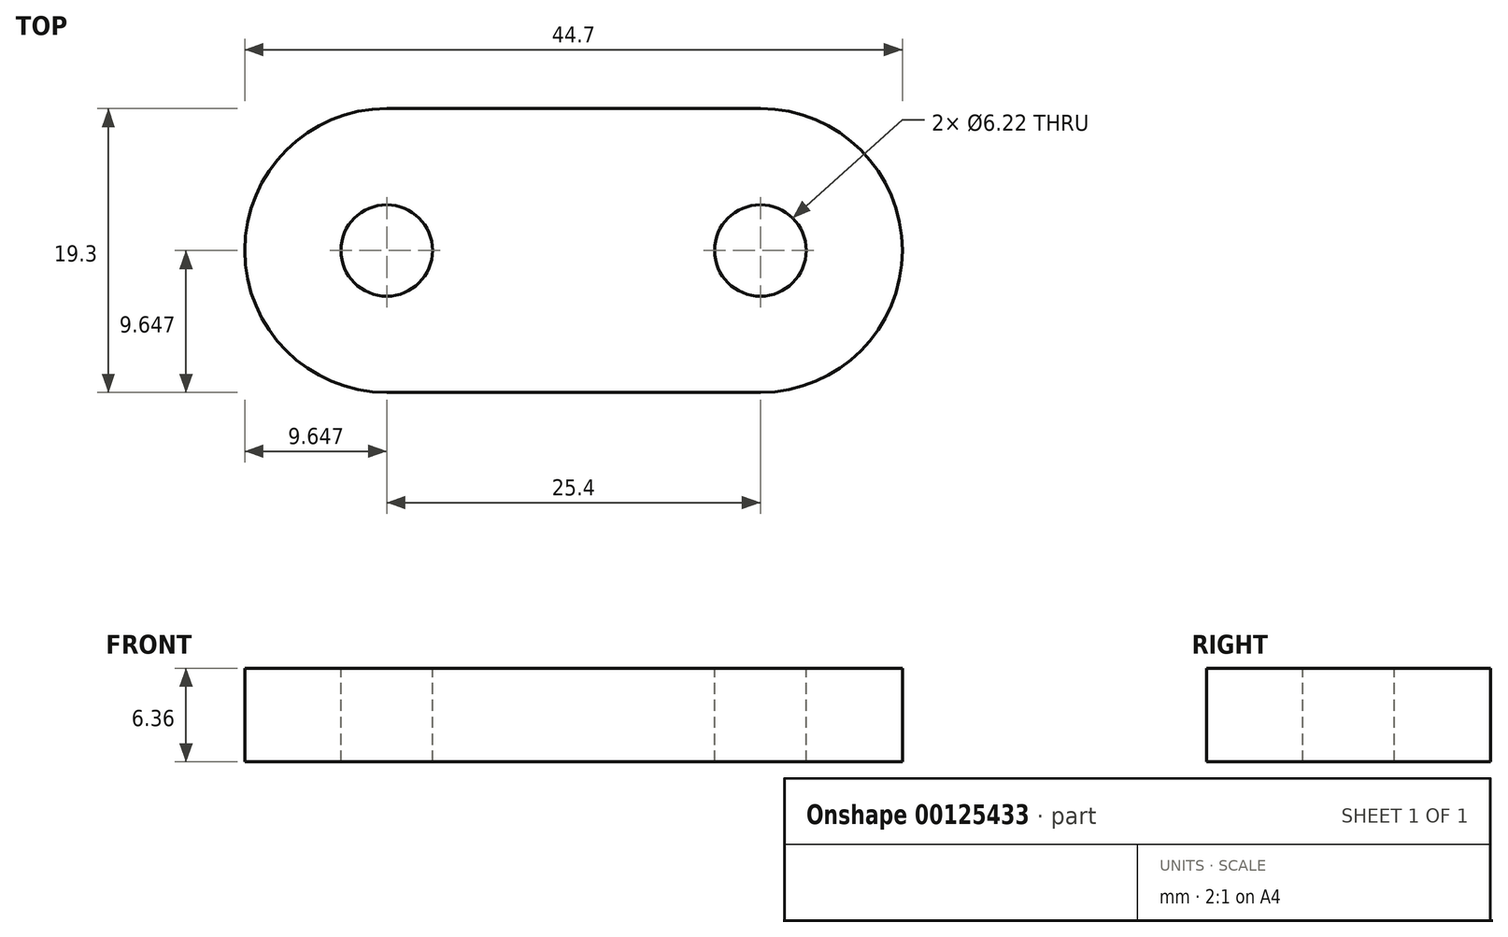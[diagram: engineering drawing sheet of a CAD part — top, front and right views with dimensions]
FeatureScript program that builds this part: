
annotation { "Feature Type Name" : "Feature", "Feature Type Description" : "" }
export const myFeature = defineFeature(function(context is Context, id is Id, definition is map)
    precondition{}
    {
        {
            var Q0;
            Q0=qCreatedBy(makeId("Top.planeOp"),FACE);
            var sketch = newSketch(context, id + "F0", { "sketchPlane" : qUnion([Q0])});
            skLineSegment(sketch, "E0", {"start": v(-28.5, 25.62) * mm, "end": v(-3.1, 25.62) * mm});
            skLineSegment(sketch, "E1", {"start": v(-28.5, 6.32) * mm, "end": v(-3.1, 6.32) * mm});
            skArc(sketch, "E2", {"start": v(-28.5, 25.62) * mm, "mid": v(-38.15, 15.97) * mm, "end": v(-28.5, 6.32) * mm});
            skArc(sketch, "E3", {"start": v(-3.1, 6.32) * mm, "mid": v(6.55, 15.97) * mm, "end": v(-3.1, 25.62) * mm});
            skCircle(sketch, "E4", {"center": v(-28.5, 15.97) * mm, "radius": 3.11 * mm});
            skCircle(sketch, "E5", {"center": v(-3.1, 15.97) * mm, "radius": 3.11 * mm});
            skSolve(sketch);
        }
        {
            var Q0;
            Q0=makeQuery(id+"F0.imprint","IMPRINT",FACE,{"disambiguationData":[TD([[makeQuery(id+"F0.imprint","IMPRINT",EDGE,{"derivedFrom":sQuery(id+"F0.wireOp",EDGE,"E0")}),-1.0]])]});
            extrude(context, id + "F1", {"entities" : qUnion([Q0]), "endBound" : BoundingType.SYMMETRIC, "oppositeDirection" : true, "depth" : 6.35 * mm});
        }
    });
